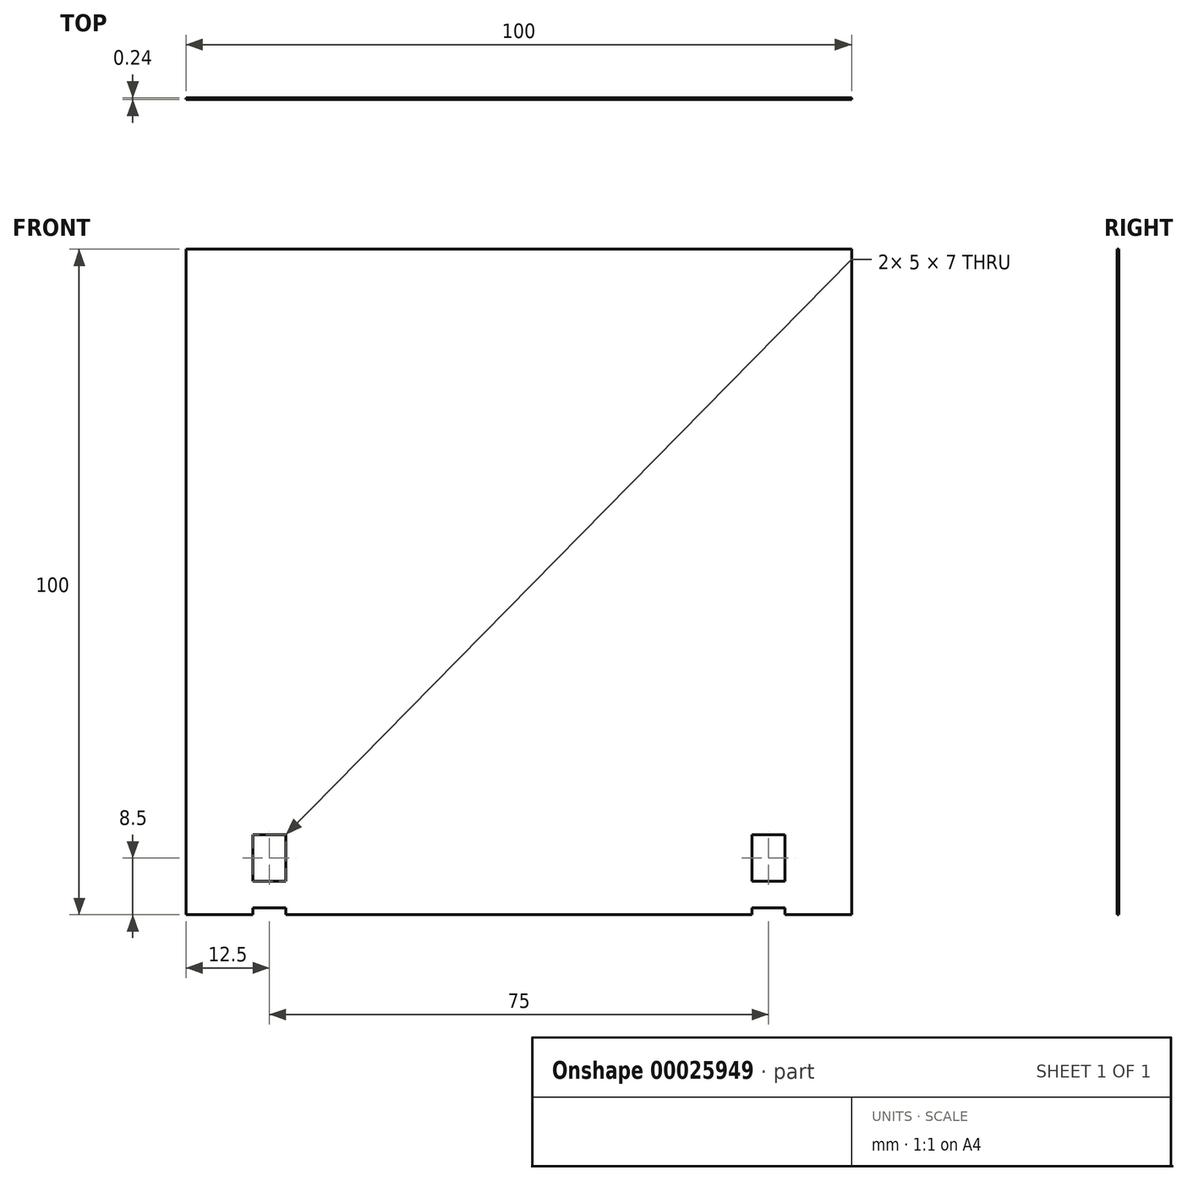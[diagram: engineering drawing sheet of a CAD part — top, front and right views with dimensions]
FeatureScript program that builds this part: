
annotation { "Feature Type Name" : "Feature", "Feature Type Description" : "" }
export const myFeature = defineFeature(function(context is Context, id is Id, definition is map)
    precondition{}
    {
        {
            var Q0;
            Q0=qCreatedBy(makeId("Front.planeOp"),FACE);
            var sketch = newSketch(context, id + "F0", { "sketchPlane" : qUnion([Q0])});
            skLineSegment(sketch, "E0.bottom", {"start": v(0, 0) * mm, "end": v(100, 0) * mm});
            skLineSegment(sketch, "E0.top", {"start": v(0, 100) * mm, "end": v(100, 100) * mm});
            skLineSegment(sketch, "E0.left", {"start": v(0, 0) * mm, "end": v(0, 100) * mm});
            skLineSegment(sketch, "E0.right", {"start": v(100, 0) * mm, "end": v(100, 100) * mm});
            skLineSegment(sketch, "E1.bottom", {"start": v(10, 0) * mm, "end": v(15, 0) * mm});
            skLineSegment(sketch, "E1.top", {"start": v(10, 1) * mm, "end": v(15, 1) * mm});
            skLineSegment(sketch, "E1.left", {"start": v(10, 0) * mm, "end": v(10, 1) * mm});
            skLineSegment(sketch, "E1.right", {"start": v(15, 0) * mm, "end": v(15, 1) * mm});
            skLineSegment(sketch, "E2.bottom", {"start": v(10, 5) * mm, "end": v(15, 5) * mm});
            skLineSegment(sketch, "E2.top", {"start": v(10, 12) * mm, "end": v(15, 12) * mm});
            skLineSegment(sketch, "E2.left", {"start": v(10, 5) * mm, "end": v(10, 12) * mm});
            skLineSegment(sketch, "E2.right", {"start": v(15, 5) * mm, "end": v(15, 12) * mm});
            skLineSegment(sketch, "E3", {"start": v(50, 100) * mm, "end": v(50, 0) * mm, "construction": true});
            skLineSegment(sketch, "E4.MirrorCS", {"start": v(90, 1) * mm, "end": v(85, 1) * mm});
            skLineSegment(sketch, "E5.MirrorCS", {"start": v(90, 0) * mm, "end": v(85, 0) * mm});
            skLineSegment(sketch, "E6.MirrorCS", {"start": v(90, 5) * mm, "end": v(90, 12) * mm});
            skLineSegment(sketch, "E7.MirrorCS", {"start": v(85, 5) * mm, "end": v(85, 12) * mm});
            skLineSegment(sketch, "E8.MirrorCS", {"start": v(90, 12) * mm, "end": v(85, 12) * mm});
            skLineSegment(sketch, "E9.MirrorCS", {"start": v(90, 0) * mm, "end": v(90, 1) * mm});
            skLineSegment(sketch, "E10.MirrorCS", {"start": v(85, 0) * mm, "end": v(85, 1) * mm});
            skLineSegment(sketch, "E11.MirrorCS", {"start": v(90, 5) * mm, "end": v(85, 5) * mm});
            skLineSegment(sketch, "E12", {"start": v(0, 3) * mm, "end": v(100, 3) * mm, "construction": true});
            skSolve(sketch);
        }
        {
            var Q0;
            Q0=makeQuery(id+"F0.imprint","IMPRINT",FACE,{"disambiguationData":[TD([[makeQuery(id+"F0.imprint","IMPRINT",EDGE,{"derivedFrom":sQuery(id+"F0.wireOp",EDGE,"E0.bottom")}),1.0]])]});
            extrude(context, id + "F1", {"entities" : qUnion([Q0]), "depth" : 0.25 * mm, "symmetric" : true});
        }
    });
